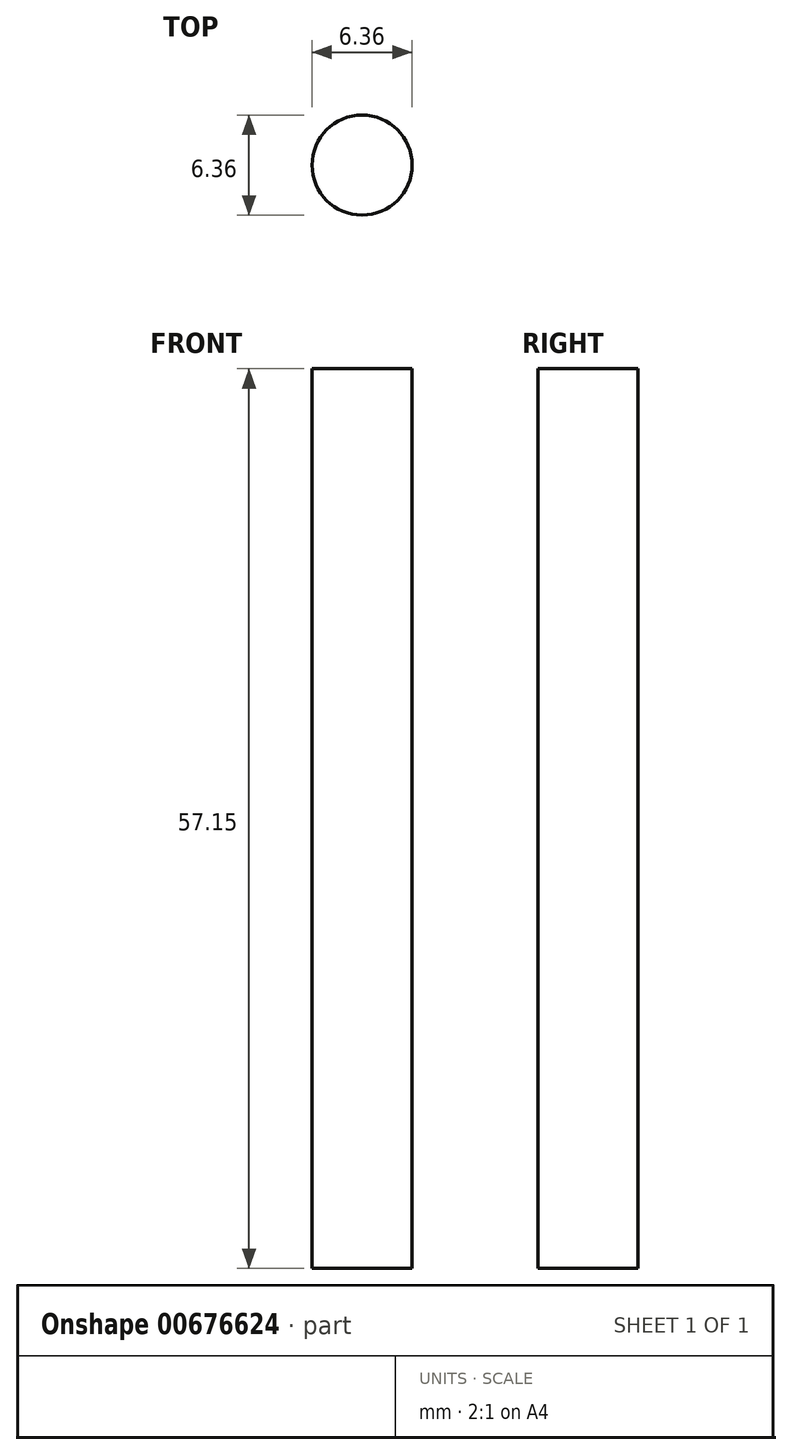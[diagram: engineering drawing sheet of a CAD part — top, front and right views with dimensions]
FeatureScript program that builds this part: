
annotation { "Feature Type Name" : "Feature", "Feature Type Description" : "" }
export const myFeature = defineFeature(function(context is Context, id is Id, definition is map)
    precondition{}
    {
        {
            var Q0;
            Q0=qCreatedBy(makeId("Top.planeOp"),FACE);
            var sketch = newSketch(context, id + "F0", { "sketchPlane" : qUnion([Q0])});
            skCircle(sketch, "E0", {"center": v(0, 0) * mm, "radius": 3.18 * mm});
            skSolve(sketch);
        }
        {
            var Q0;
            Q0=qSketchRegion(id+"F0",true);
            extrude(context, id + "F1", {"entities" : qUnion([Q0]), "depth" : 57.15 * mm});
        }
    });
